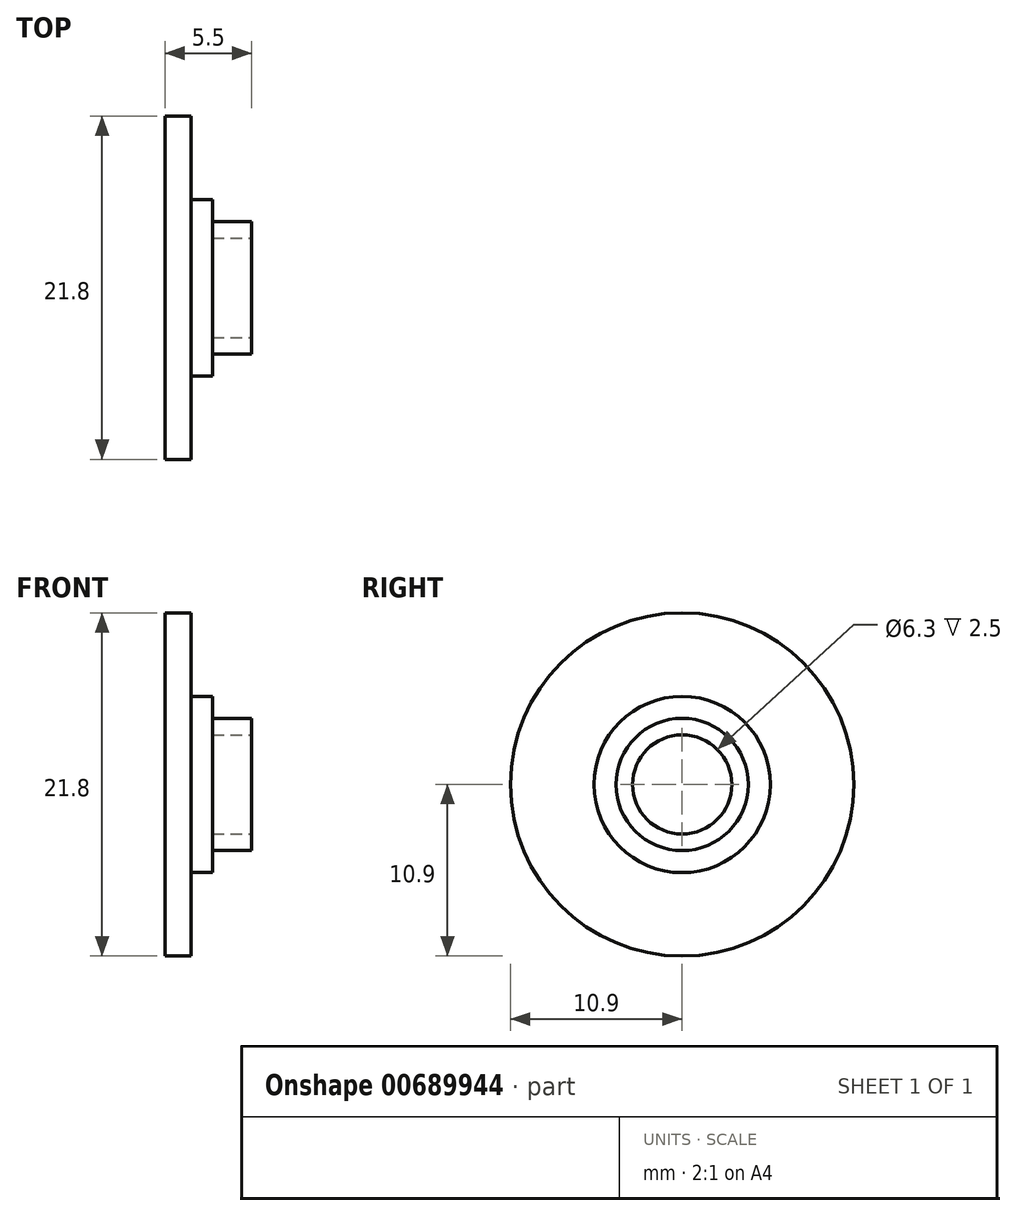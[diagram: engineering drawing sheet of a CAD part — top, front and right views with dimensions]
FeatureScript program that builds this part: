
annotation { "Feature Type Name" : "Feature", "Feature Type Description" : "" }
export const myFeature = defineFeature(function(context is Context, id is Id, definition is map)
    precondition{}
    {
        {
            var Q0;
            Q0=qCreatedBy(makeId("Right.planeOp"),FACE);
            var sketch = newSketch(context, id + "F0", { "sketchPlane" : qUnion([Q0])});
            skCircle(sketch, "E0", {"center": v(0, 0) * mm, "radius": 10.9 * mm});
            skSolve(sketch);
        }
        {
            var Q0;
            Q0=makeQuery(id+"F0.imprint","IMPRINT",FACE,{"disambiguationData":[TD([[makeQuery(id+"F0.imprint","IMPRINT",EDGE,{"derivedFrom":sQuery(id+"F0.wireOp",EDGE,"E0")}),1.0]])]});
            var Q1;
            Q1=qSketchRegion(id+"F2",true);
            extrude(context, id + "F1", {"entities" : qUnion([Q0, Q1]), "depth" : 1.65 * mm, "offsetDistance" : 25 * mm});
        }
        {
            var Q0;
            Q0=qCreatedBy(makeId("Right.planeOp"),FACE);
            var sketch = newSketch(context, id + "F2", { "sketchPlane" : qUnion([Q0])});
            skCircle(sketch, "E1", {"center": v(0, 0) * mm, "radius": 4.2 * mm});
            skSolve(sketch);
        }
        {
            var Q0;
            Q0=qSketchRegion(id+"F2",true);
            extrude(context, id + "F3", {"entities" : qUnion([Q0]), "operationType" : NewBodyOperationType.ADD, "depth" : 5.5 * mm, "offsetDistance" : 25 * mm});
        }
        {
            var Q0;
            Q0=makeQuery(id+"F3.opExtrude","CAP_FACE",FACE,{"disambiguationData":[OSD([sQuery(id+"F2.wireOp",EDGE,"E1")])],"isStart":false});
            cPlane(context, id + "F4", {"entities" : qUnion([Q0]), "cplaneType" : CPlaneType.OFFSET, "offset" : 0 * mm, "width" : 150 * mm, "height" : 150 * mm});
        }
        {
            var Q0;
            Q0=qCreatedBy(id+"F4.planeOp",FACE);
            var sketch = newSketch(context, id + "F5", { "sketchPlane" : qUnion([Q0])});
            skCircle(sketch, "E2", {"center": v(0, 0) * mm, "radius": 3.15 * mm});
            skSolve(sketch);
        }
        {
            var Q0;
            Q0=makeQuery(id+"F5.imprint","IMPRINT",FACE,{"disambiguationData":[TD([[makeQuery(id+"F5.imprint","IMPRINT",EDGE,{"derivedFrom":sQuery(id+"F5.wireOp",EDGE,"E2")}),1.0]])]});
            extrude(context, id + "F6", {"entities" : qUnion([Q0]), "operationType" : NewBodyOperationType.REMOVE, "oppositeDirection" : true, "depth" : 3.37 * mm, "offsetDistance" : 25 * mm});
        }
        {
            var Q0;
            Q0=qCreatedBy(makeId("Right.planeOp"),FACE);
            var sketch = newSketch(context, id + "F7", { "sketchPlane" : qUnion([Q0])});
            skCircle(sketch, "E3", {"center": v(0, 0) * mm, "radius": 3.18 * mm});
            skSolve(sketch);
        }
        {
            var Q0;
            Q0=qSketchRegion(id+"F7",true);
            extrude(context, id + "F8", {"entities" : qUnion([Q0]), "operationType" : NewBodyOperationType.ADD, "depth" : 1.65 * mm, "offsetDistance" : 25 * mm});
        }
        {
            var Q0;
            Q0=qCreatedBy(makeId("Right.planeOp"),FACE);
            var sketch = newSketch(context, id + "F9", { "sketchPlane" : qUnion([Q0])});
            skCircle(sketch, "E4", {"center": v(0, 0) * mm, "radius": 5.6 * mm});
            skSolve(sketch);
        }
        {
            var Q0;
            Q0=qSketchRegion(id+"F9",true);
            extrude(context, id + "F10", {"entities" : qUnion([Q0]), "operationType" : NewBodyOperationType.ADD, "depth" : 3 * mm, "offsetDistance" : 25 * mm});
        }
    });
